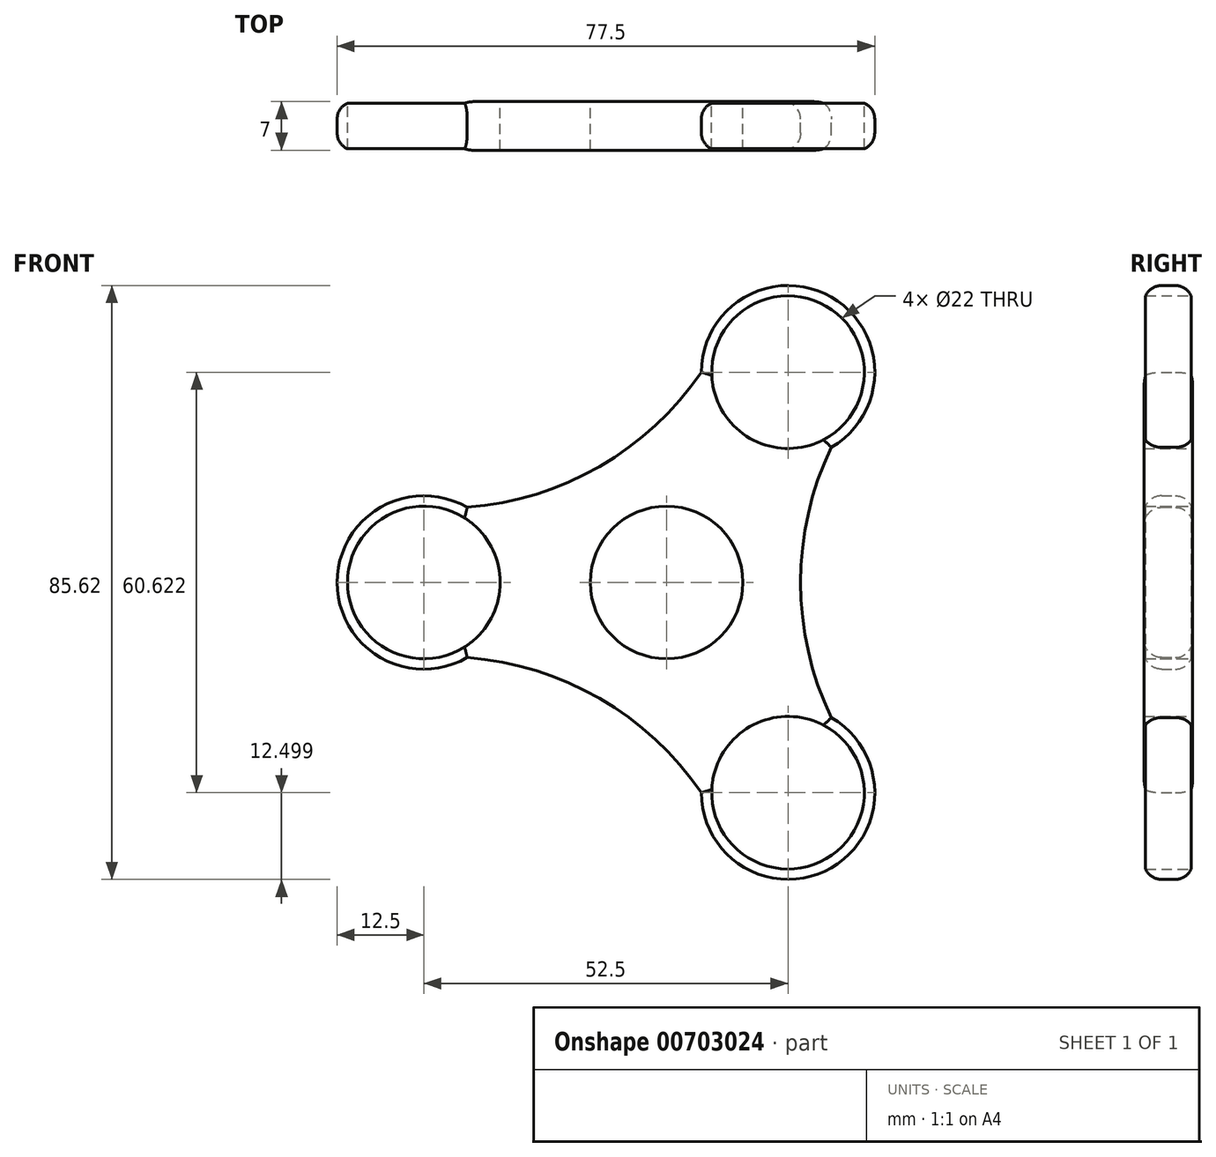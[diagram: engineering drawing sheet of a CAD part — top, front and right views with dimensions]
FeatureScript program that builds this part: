
annotation { "Feature Type Name" : "Feature", "Feature Type Description" : "" }
export const myFeature = defineFeature(function(context is Context, id is Id, definition is map)
    precondition{}
    {
        {
            var Q0;
            Q0=qCreatedBy(makeId("Front.planeOp"),FACE);
            var sketch = newSketch(context, id + "F0", { "sketchPlane" : qUnion([Q0])});
            skCircle(sketch, "E0", {"center": v(0, 0) * mm, "radius": 11 * mm});
            skCircle(sketch, "E1", {"center": v(17.5, 30.31) * mm, "radius": 11 * mm});
            skCircle(sketch, "E2", {"center": v(-35, 0) * mm, "radius": 11 * mm});
            skCircle(sketch, "E3", {"center": v(17.5, -30.31) * mm, "radius": 11 * mm});
            skArc(sketch, "E4", {"start": v(5, -30.31) * mm, "mid": v(23.75, -41.14) * mm, "end": v(23.75, -19.49) * mm});
            skArc(sketch, "E5", {"start": v(23.75, 19.49) * mm, "mid": v(23.75, 41.14) * mm, "end": v(5, 30.31) * mm});
            skArc(sketch, "E6", {"start": v(-28.75, 10.83) * mm, "mid": v(-47.5, 0) * mm, "end": v(-28.75, -10.83) * mm});
            skArc(sketch, "E7", {"start": v(5, -30.31) * mm, "mid": v(-9.66, -16.73) * mm, "end": v(-28.75, -10.83) * mm});
            skArc(sketch, "E8", {"start": v(-28.75, 10.83) * mm, "mid": v(-9.66, 16.73) * mm, "end": v(5, 30.31) * mm});
            skArc(sketch, "E9", {"start": v(23.75, 19.49) * mm, "mid": v(19.31, 0) * mm, "end": v(23.75, -19.49) * mm});
            skSolve(sketch);
        }
        {
            var Q0;
            Q0 = qSketchRegion(id + "F0", true);
            extrude(context, id + "F1", {"entities" : qUnion([Q0]), "depth" : 7 * mm, "offsetDistance" : 25 * mm});
        }
        {
            var Q0;
            Q0=makeQuery(id+"F1.opExtrude","CAP_EDGE",EDGE,{"disambiguationData":[OSD([sQuery(id+"F0.wireOp",EDGE,"E7")])],"isStart":false});
            var Q1;
            Q1=makeQuery(id+"F1.opExtrude","CAP_EDGE",EDGE,{"disambiguationData":[OSD([sQuery(id+"F0.wireOp",EDGE,"E4")])],"isStart":false});
            var Q2;
            Q2=makeQuery(id+"F1.opExtrude","CAP_EDGE",EDGE,{"disambiguationData":[OSD([sQuery(id+"F0.wireOp",EDGE,"E9")])],"isStart":false});
            var Q3;
            Q3=makeQuery(id+"F1.opExtrude","CAP_EDGE",EDGE,{"disambiguationData":[OSD([sQuery(id+"F0.wireOp",EDGE,"E5")])],"isStart":false});
            var Q4;
            Q4=makeQuery(id+"F1.opExtrude","CAP_EDGE",EDGE,{"disambiguationData":[OSD([sQuery(id+"F0.wireOp",EDGE,"E8")])],"isStart":false});
            var Q5;
            Q5=makeQuery(id+"F1.opExtrude","CAP_EDGE",EDGE,{"disambiguationData":[OSD([sQuery(id+"F0.wireOp",EDGE,"E6")])],"isStart":false});
            fillet(context, id + "F2", {"entities" : qUnion([Q0, Q1, Q2, Q3, Q4, Q5]), "radius" : 2.5 * mm, "tangentPropagation" : true, "allowEdgeOverflow" : false});
        }
        {
            var Q0;
            Q0=makeQuery(id+"F1.opExtrude","CAP_EDGE",EDGE,{"disambiguationData":[OSD([sQuery(id+"F0.wireOp",EDGE,"E5")])],"isStart":true});
            var Q1;
            Q1=makeQuery(id+"F1.opExtrude","CAP_EDGE",EDGE,{"disambiguationData":[OSD([sQuery(id+"F0.wireOp",EDGE,"E8")])],"isStart":true});
            var Q2;
            Q2=makeQuery(id+"F1.opExtrude","CAP_EDGE",EDGE,{"disambiguationData":[OSD([sQuery(id+"F0.wireOp",EDGE,"E6")])],"isStart":true});
            var Q3;
            Q3=makeQuery(id+"F1.opExtrude","CAP_EDGE",EDGE,{"disambiguationData":[OSD([sQuery(id+"F0.wireOp",EDGE,"E7")])],"isStart":true});
            var Q4;
            Q4=makeQuery(id+"F1.opExtrude","CAP_EDGE",EDGE,{"disambiguationData":[OSD([sQuery(id+"F0.wireOp",EDGE,"E4")])],"isStart":true});
            var Q5;
            Q5=makeQuery(id+"F1.opExtrude","CAP_EDGE",EDGE,{"disambiguationData":[OSD([sQuery(id+"F0.wireOp",EDGE,"E9")])],"isStart":true});
            fillet(context, id + "F3", {"entities" : qUnion([Q0, Q1, Q2, Q3, Q4, Q5]), "radius" : 2.5 * mm, "tangentPropagation" : true, "allowEdgeOverflow" : false});
        }
    });
